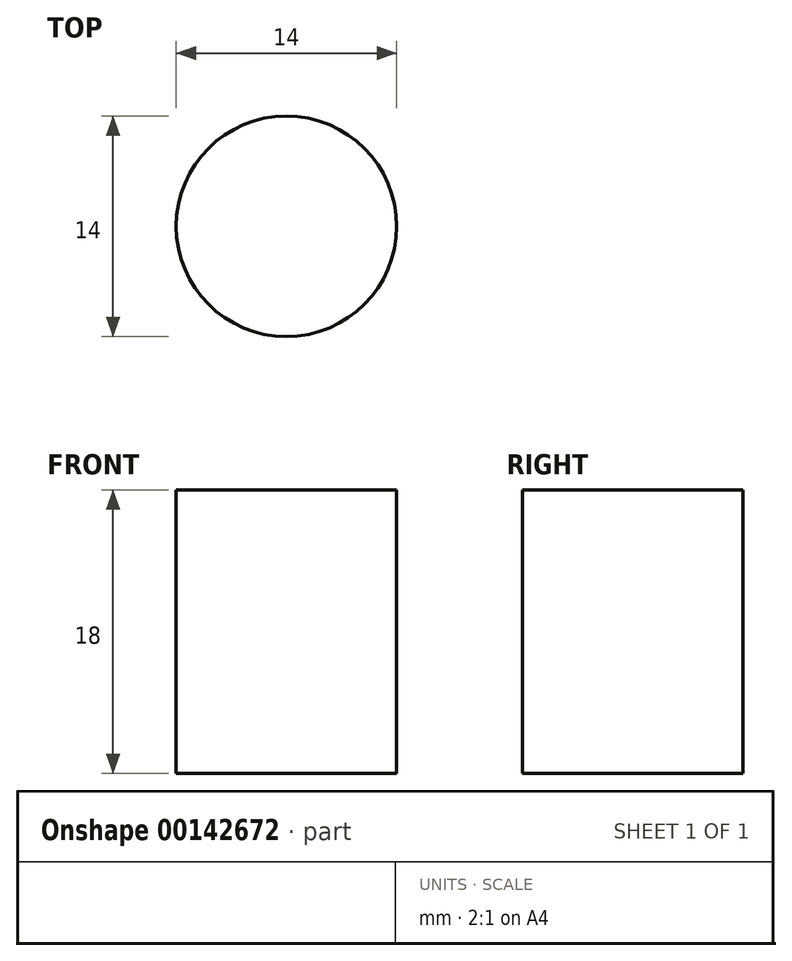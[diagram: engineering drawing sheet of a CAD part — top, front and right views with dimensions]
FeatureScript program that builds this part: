
annotation { "Feature Type Name" : "Feature", "Feature Type Description" : "" }
export const myFeature = defineFeature(function(context is Context, id is Id, definition is map)
    precondition{}
    {
        {
            var Q0;
            Q0=qCreatedBy(makeId("Top.planeOp"),FACE);
            var sketch = newSketch(context, id + "F0", { "sketchPlane" : qUnion([Q0])});
            skCircle(sketch, "E0", {"center": v(0, 0) * mm, "radius": 7 * mm});
            skSolve(sketch);
        }
        {
            var Q0;
            Q0 = qSketchRegion(id + "F0", true);
            extrude(context, id + "F1", {"entities" : qUnion([Q0]), "depth" : 18 * mm});
        }
    });
